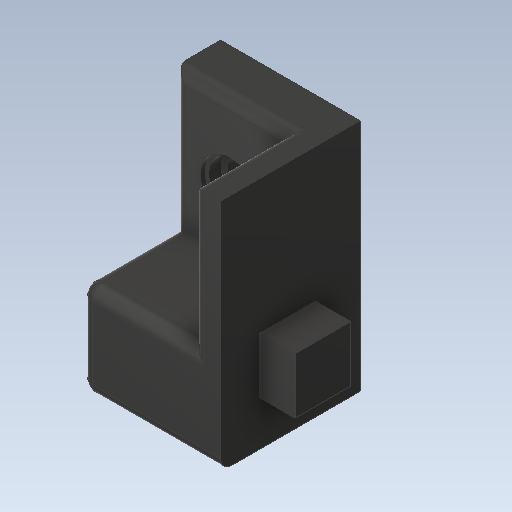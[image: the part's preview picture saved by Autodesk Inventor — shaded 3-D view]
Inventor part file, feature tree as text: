
AUTODESK INVENTOR PART (.ipt)
format: ipt  version: 2020 (Build 240168000, 168)  size: 252,928 bytes
history: native  units: in
note: dims shown in document units (in); Inventor stores cm internally (conversion verified against a paired STEP export)
features: sketch x13, extrude x12, projected_geometry x10, fillet x3, chamfer x1
ambient origin geometry x8: Origin, YZ Plane, XZ Plane, XY Plane, X Axis, Y Axis, Z Axis, Center Point
bodies: Solid1 (feature_tree)
feature tree (39):
  extrude  "Extrusion1"  Depth=0.9843in
  extrude  "Extrusion2"  TaperAngle=0.0deg  [1 undecoded]
  extrude  "Extrusion3"  TaperAngle=90.0deg  [1 undecoded]
  extrude  "Extrusion4"  Depth=0.7874in TaperAngle=0.0deg
  extrude  "Extrusion6"  Depth=0.7874in TaperAngle=0.0deg
  extrude  "Extrusion8"  Depth=0.126in TaperAngle=0.0deg
  extrude  "Extrusion10"  Depth=0.0362in TaperAngle=0.0deg
  extrude  "Extrusion11"  Depth=0.3937in TaperAngle=0.0deg
  extrude  "Extrusion12"  Depth=0.4724in TaperAngle=0.0deg
  fillet  "Fillet3"  Radius=0.4724in
  extrude  "Extrusion9"  Depth=0.0787in
  fillet  "Fillet1"  Radius=0.0787in
  fillet  "Fillet2"  Radius=0.748in
  chamfer  "Chamfer1"  Distance=0.2461in
  sketch  "Sketch7"  dims[d16=0.4244in d17=0.0362in d18=0.0in]
  extrude  "Extrusion7"  Depth=0.3937in TaperAngle=0.0deg
  extrude  "Extrusion5"  Depth=0.3937in
  sketch  "Sketch1"  dims[d0=0.6693in d1=0.9843in]
  sketch  "Sketch2"  dims[d2=0.9843in d3=0.0in]
  sketch  "Sketch3"  dims[d4=0.3248in d5=90.0deg]
  sketch  "Sketch4"  dims[d6=180.0deg d7=0.7874in d8=0.0in]
  sketch  "Sketch5"  dims[d9=0.3in d11=0.7874in d12=0.0in]
  sketch  "Sketch6"  dims[d13=0.3791in d14=0.126in d15=0.0in]
  projected_geometry  "Projected Loop1"
  projected_geometry  "Projected Loop2"
  projected_geometry  "Projected Loop3"
  sketch  "Sketch8"  dims[d19=0.3189in d20=0.3937in d21=0.0in]
  projected_geometry  "Projected Loop4"
  projected_geometry  "Projected Loop5"
  sketch  "Sketch9"  dims[d22=0.492in d23=1.0in d24=0.0in d25=0.4724in]
  sketch  "Sketch10"  dims[d26=0.3937in d27=0.2362in d28=0.0787in]
  projected_geometry  "Projected Loop6"
  sketch  "Sketch12"  dims[d29=0.0787in d30=0.0787in d31=45.0deg d32=0.748in]
  projected_geometry  "Projected Loop7"
  sketch  "Sketch14"  dims[d33=1.0827in]
  projected_geometry  "Projected Loop8"
  sketch  "Sketch15"  dims[d34=0.3189in d35=0.2461in d36=0.3937in d37=0.0in d38=0.3937in d39=0.3937in d40=0.1969in d41=0.3937in d42=0.25in d43=0.0in d44=0.3937in d45=0.3937in d46=0.1969in d47=0.1969in d48=0.25in d49=0.0in d50=0.1969in d51=0.0in d52=0.3346in d53=0.3228in d54=0.4016in d55=0.0in d56=0.3937in d57=0.3937in d58=0.315in d59=0.315in d60=0.25in d61=0.0in d62=0.0787in]
  projected_geometry  "Projected Loop9"
  projected_geometry  "Projected Loop10"
note: 2 required parameter values undecoded (feature->parameter linkage not recoverable at this tier; creation-order binding heuristic only, values carry confidence <= 0.55)
